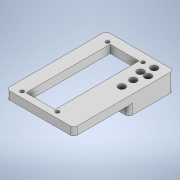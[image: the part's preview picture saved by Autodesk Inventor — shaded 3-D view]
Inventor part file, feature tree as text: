
AUTODESK INVENTOR PART (.ipt)
format: ipt  version: 2021 (Build 250183000, 183)  size: 196,096 bytes
history: native  units: in
note: dims shown in document units (in); Inventor stores cm internally (conversion verified against a paired STEP export)
features: sketch x5, extrude x4, fillet x1
ambient origin geometry x8: Origin, YZ Plane, XZ Plane, XY Plane, X Axis, Y Axis, Z Axis, Center Point
bodies: Solid1 (feature_tree)
feature tree (10):
  extrude  "Extrusion1"  Depth=1.0in
  extrude  "Extrusion3"  Depth=1.375in
  extrude  "Extrusion2"  Depth=0.125in
  extrude  "Extrusion5"  Depth=0.125in
  sketch  "Sketch4"  dims[d8=0.125in d9=0.125in d10=0.125in]
  fillet  "Fillet1"  Radius=0.125in
  sketch  "Sketch1"  dims[d0=2.9in d1=1.0in]
  sketch  "Sketch2"  dims[d4=3.35in d5=1.375in]
  sketch  "Sketch3"  dims[d6=2.335in d7=0.125in]
  sketch  "Sketch7"  dims[d11=0.2in d12=0.35in d13=0.2in d14=0.765in d15=0.275in d16=0.0in d17=0.2375in d18=0.2375in d19=0.2375in d20=0.2375in d21=0.265in d22=0.405in d23=0.525in d24=0.2375in d25=0.175in d26=0.72in d27=0.35in d28=1.113in d29=0.0in d30=0.0in d31=1.45in d32=0.675in d33=0.35in d34=0.0in d35=0.45in d36=0.45in d37=0.45in d38=0.45in d39=0.45in d42=0.1in d43=0.0in d46=0.125in d44=0.5in d45=0.0344in d47=0.0344in d48=0.5in d49=0.0344in]
